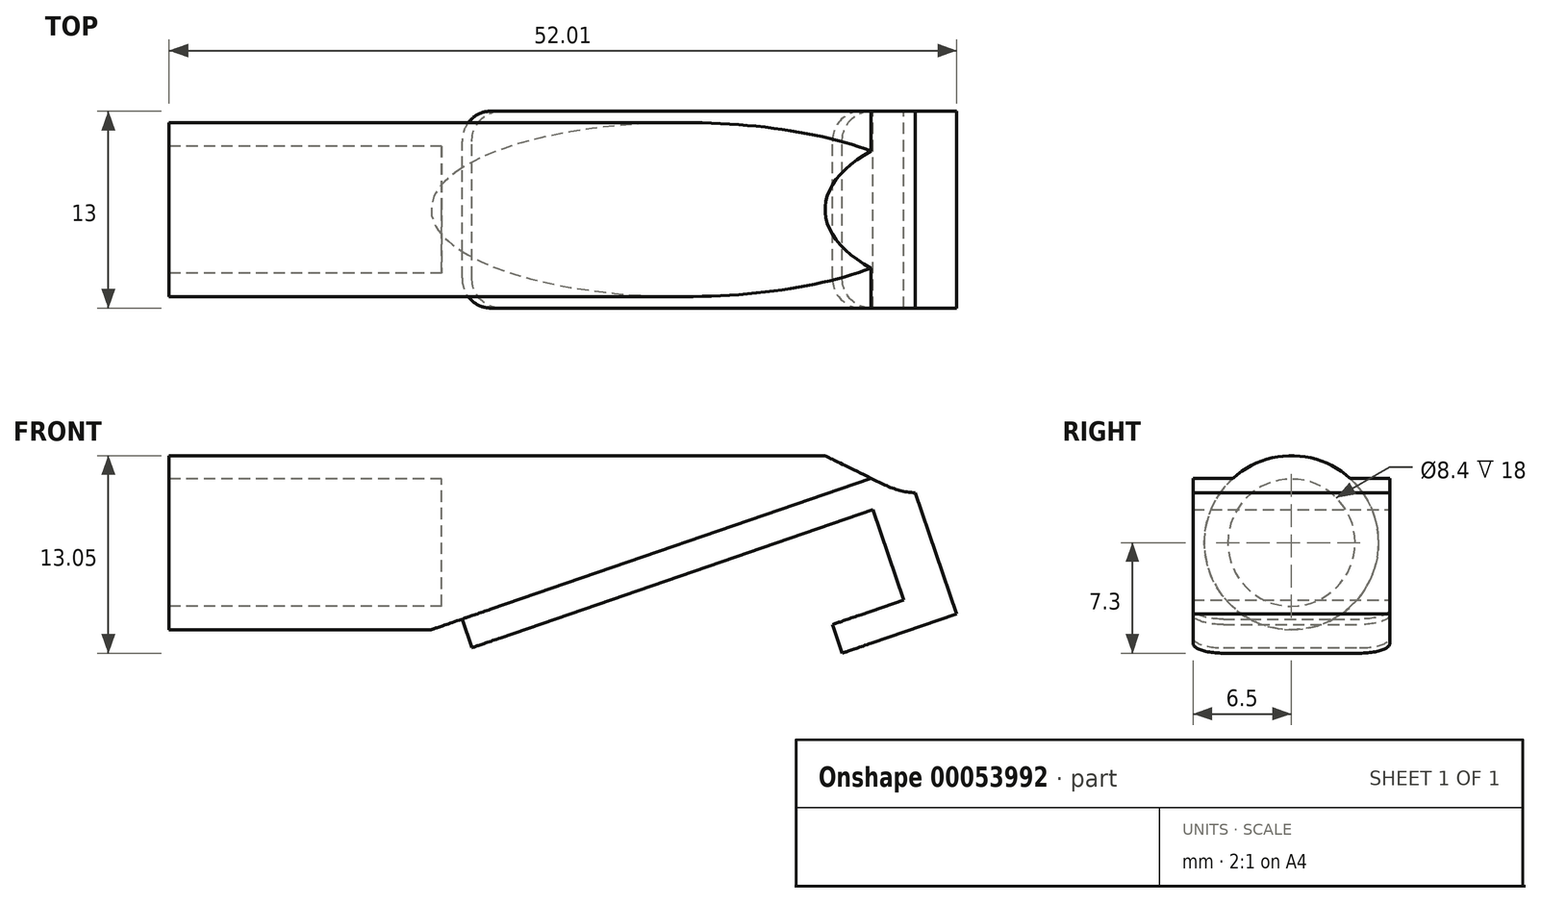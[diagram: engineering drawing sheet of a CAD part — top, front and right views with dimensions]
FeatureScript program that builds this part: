
annotation { "Feature Type Name" : "Feature", "Feature Type Description" : "" }
export const myFeature = defineFeature(function(context is Context, id is Id, definition is map)
    precondition{}
    {
        {
            var Q0;
            Q0=qCreatedBy(makeId("Front.planeOp"),FACE);
            var sketch = newSketch(context, id + "F0", { "sketchPlane" : qUnion([Q0])});
            skLineSegment(sketch, "E0", {"start": v(1.34, -5.05) * mm, "end": v(30.66, 5.05) * mm});
            skLineSegment(sketch, "E1", {"start": v(30.66, 5.05) * mm, "end": v(34, -4.7) * mm});
            skLineSegment(sketch, "E2", {"start": v(34, -4.7) * mm, "end": v(26.44, -7.3) * mm});
            skLineSegment(sketch, "E3", {"start": v(26.44, -7.3) * mm, "end": v(25.8, -5.4) * mm});
            skLineSegment(sketch, "E4", {"start": v(25.8, -5.4) * mm, "end": v(30.52, -3.78) * mm});
            skLineSegment(sketch, "E5", {"start": v(30.52, -3.78) * mm, "end": v(28.47, 2.18) * mm});
            skLineSegment(sketch, "E6", {"start": v(28.47, 2.18) * mm, "end": v(2, -6.94) * mm});
            skLineSegment(sketch, "E7", {"start": v(2, -6.94) * mm, "end": v(1.34, -5.05) * mm});
            skPoint(sketch, "E8", {"position": v(16, 0) * mm});
            skSolve(sketch);
        }
        {
            var Q0;
            Q0=makeQuery(id+"F0.imprint","IMPRINT",FACE,{"disambiguationData":[TD([[makeQuery(id+"F0.imprint","IMPRINT",EDGE,{"derivedFrom":sQuery(id+"F0.wireOp",EDGE,"E0")}),-1.0]])]});
            extrude(context, id + "F1", {"entities" : qUnion([Q0]), "endBound" : BoundingType.SYMMETRIC, "depth" : 13 * mm, "hasSecondDirection" : true, "secondDirectionOppositeDirection" : true, "secondDirectionDepth" : 5 * mm});
        }
        {
            var Q0;
            Q0=qCreatedBy(makeId("Right.planeOp"),FACE);
            var sketch = newSketch(context, id + "F2", { "sketchPlane" : qUnion([Q0])});
            skCircle(sketch, "E9", {"center": v(0, 0) * mm, "radius": 4.2 * mm});
            skCircle(sketch, "E10", {"center": v(0, 0) * mm, "radius": 5.75 * mm});
            skSolve(sketch);
        }
        {
            var Q0;
            Q0=makeQuery(id+"F2.imprint","IMPRINT",FACE,{"disambiguationData":[TD([[makeQuery(id+"F2.imprint","IMPRINT",EDGE,{"derivedFrom":sQuery(id+"F2.wireOp",EDGE,"E9")}),-1.0]])]});
            var Q1;
            Q1=makeQuery(id+"F1.opExtrude","SWEPT_FACE",FACE,{"disambiguationData":[OSD([sQuery(id+"F0.wireOp",EDGE,"E0")])]});
            extrude(context, id + "F3", {"entities" : qUnion([Q0]), "operationType" : NewBodyOperationType.ADD, "endBound" : BoundingType.UP_TO_SURFACE, "endBoundEntityFace" : qUnion([Q1]), "depth" : 25 * mm, "hasSecondDirection" : true, "secondDirectionOppositeDirection" : true, "secondDirectionDepth" : 18 * mm});
        }
        {
            var Q0;
            {var subQ0=sQuery(id+"F2.wireOp",EDGE,"E10");Q0=makeQuery(id+"F3.boolean.opBoolean","SPLIT",FACE,{"disambiguationData":[TD([makeQuery(id+"F1.opExtrude","SWEPT_FACE",FACE,{"disambiguationData":[OSD([sQuery(id+"F0.wireOp",EDGE,"E1")])]})])],"derivedFrom":makeQuery(id+"F3.opExtrude","CAP_FACE",FACE,{"disambiguationData":[OSD([sQuery(id+"F2.wireOp",EDGE,"E9"),subQ0])],"isStart":false})});}
            var sketch = newSketch(context, id + "F4", { "sketchPlane" : qUnion([Q0])});
            skEllipticalArc(sketch, "E11.1", {});
            skLineSegment(sketch, "E12.2", {"start": v(30.63, 2.76) * mm, "end": v(30.63, -2.76) * mm});
            const initialGuessF4  = {"E11.1": [0.015128297209500065, 0, -1, 0, 0.016125655805475526, 0.00525, 2.8621206456342367, 3.4210646615643387], "E11.1": [0.015128297209500065, 0, -1, 0, 0.016125655805475526, 0.00525, 2.8621206456342367, 3.4210646615643387]};
            skSetInitialGuess(sketch, initialGuessF4);
            skSolve(sketch);
        }
        {
            var Q0;
            Q0=makeQuery(id+"F4.imprint","IMPRINT",FACE,{"disambiguationData":[TD([[makeQuery(id+"F4.imprint","IMPRINT",EDGE,{"derivedFrom":sQuery(id+"F4.wireOp",EDGE,"E11.1")}),-1.0]])]});
            extrude(context, id + "F5", {"entities" : qUnion([Q0]), "operationType" : NewBodyOperationType.REMOVE, "endBound" : BoundingType.THROUGH_ALL, "oppositeDirection" : true, "depth" : 25 * mm});
        }
        {
            var Q0;
            Q0=makeQuery(id+"F1.opExtrude","CAP_EDGE",EDGE,{"disambiguationData":[OSD([sQuery(id+"F0.wireOp",EDGE,"E3")])],"isStart":true});
            var Q1;
            Q1=makeQuery(id+"F1.opExtrude","CAP_EDGE",EDGE,{"disambiguationData":[OSD([sQuery(id+"F0.wireOp",EDGE,"E3")])],"isStart":false});
            var Q2;
            Q2=makeQuery(id+"F1.opExtrude","CAP_EDGE",EDGE,{"disambiguationData":[OSD([sQuery(id+"F0.wireOp",EDGE,"E7")])],"isStart":false});
            var Q3;
            Q3=makeQuery(id+"F1.opExtrude","CAP_EDGE",EDGE,{"disambiguationData":[OSD([sQuery(id+"F0.wireOp",EDGE,"E7")])],"isStart":true});
            fillet(context, id + "F6", {"entities" : qUnion([Q0, Q1, Q2, Q3]), "radius" : 2 * mm, "tangentPropagation" : true, "allowEdgeOverflow" : false});
        }
        {
            var Q0;
            Q0=qCreatedBy(makeId("Front.planeOp"),FACE);
            var sketch = newSketch(context, id + "F7", { "sketchPlane" : qUnion([Q0])});
            skArc(sketch, "E13", {"start": v(29.27, 3.82) * mm, "mid": v(36.29, 6.23) * mm, "end": v(33.87, 13.25) * mm});
            skLineSegment(sketch, "E14", {"start": v(29.27, 3.82) * mm, "end": v(23.2, 6.77) * mm});
            skLineSegment(sketch, "E15", {"start": v(23.2, 6.77) * mm, "end": v(27.8, 16.21) * mm});
            skLineSegment(sketch, "E16", {"start": v(27.8, 16.21) * mm, "end": v(33.87, 13.25) * mm});
            skSolve(sketch);
        }
        {
            var Q0;
            Q0=makeQuery(id+"F7.imprint","IMPRINT",FACE,{"disambiguationData":[TD([[makeQuery(id+"F7.imprint","IMPRINT",EDGE,{"derivedFrom":sQuery(id+"F7.wireOp",EDGE,"E13")}),1.0]])]});
            extrude(context, id + "F8", {"entities" : qUnion([Q0]), "operationType" : NewBodyOperationType.REMOVE, "endBound" : BoundingType.THROUGH_ALL, "oppositeDirection" : true, "depth" : 25 * mm, "hasSecondDirection" : true, "secondDirectionBound" : SecondDirectionBoundingType.THROUGH_ALL, "secondDirectionOppositeDirection" : false, "secondDirectionDepth" : 25 * mm});
        }
        {
            var Q0;
            Q0=qCreatedBy(makeId("Right.planeOp"),FACE);
            var sketch = newSketch(context, id + "F9", { "sketchPlane" : qUnion([Q0])});
            skCircle(sketch, "E17.0", {"center": v(0, 0) * mm, "radius": 4.2 * mm});
            skSolve(sketch);
        }
        {
            var Q0;
            Q0=qSketchRegion(id+"F9",true);
            var Q1;
            Q1=makeQuery(id+"F3.boolean.opBoolean","SPLIT",FACE,{"disambiguationData":[TD([makeQuery(id+"F3.opExtrude","SWEPT_FACE",FACE,{"disambiguationData":[OSD([sQuery(id+"F2.wireOp",EDGE,"E9")])]})])],"derivedFrom":makeQuery(id+"F1.opExtrude","SWEPT_FACE",FACE,{"disambiguationData":[OSD([sQuery(id+"F0.wireOp",EDGE,"E0")])]})});
            extrude(context, id + "F10", {"entities" : qUnion([Q0]), "operationType" : NewBodyOperationType.ADD, "endBound" : BoundingType.UP_TO_SURFACE, "endBoundEntityFace" : qUnion([Q1]), "depth" : 25 * mm});
        }
    });
